# Revit family: LIPROOF105_LIPROOF105HO
name_source: partatom
category: Lighting Fixtures
units: mm (PartAtom-declared; Revit-internal decimal feet)

## family parameters
Cut with Voids When Loaded = No
Host = Face
Light Source = Yes
Maintain Annotation Orientation = Yes
Part Type = Normal
Room Calculation Point = No
Round Connector Dimension = Use Diameter
Shared = No

## types (2) — shared parameters
Color Filter = 16777215
Default Elevation = 1219 mm
Dimming Lamp Color Temperature Shift = <None>
Emit from Line Length = 610 mm
LuxLight_Largo = 1500 mm
LuxLight_Lumenes = 5900 lm
Manufacturer = LUXLIGHT
Tilt Angle = 0.00°
zero-valued in all types: LuxLight_Alto, LuxLight_AltoAreaLuminosa, LuxLight_Amperios, LuxLight_Ancho, LuxLight_AnchoAreaLuminosa, LuxLight_Diametro, LuxLight_DiametroAreaLuminosa, LuxLight_LargoAreaLuminosa, LuxLight_ProtuberanciaTecho

## per-type parameters (varying)
| type | LuxLight_Temperatura | LuxLight_Watios | Photometric Web File |
| LIPROOF105HO | 0 K | 0 W | LIPROOF105HO 80W 4000K .ies |
| LIPROOF105 | 3000 K | 24 W | LIPROOF105 48W 4000K .ies |

## geometry (parser evidence)
native form markers: Sweep x8
no freeform markers — native parametric forms only
